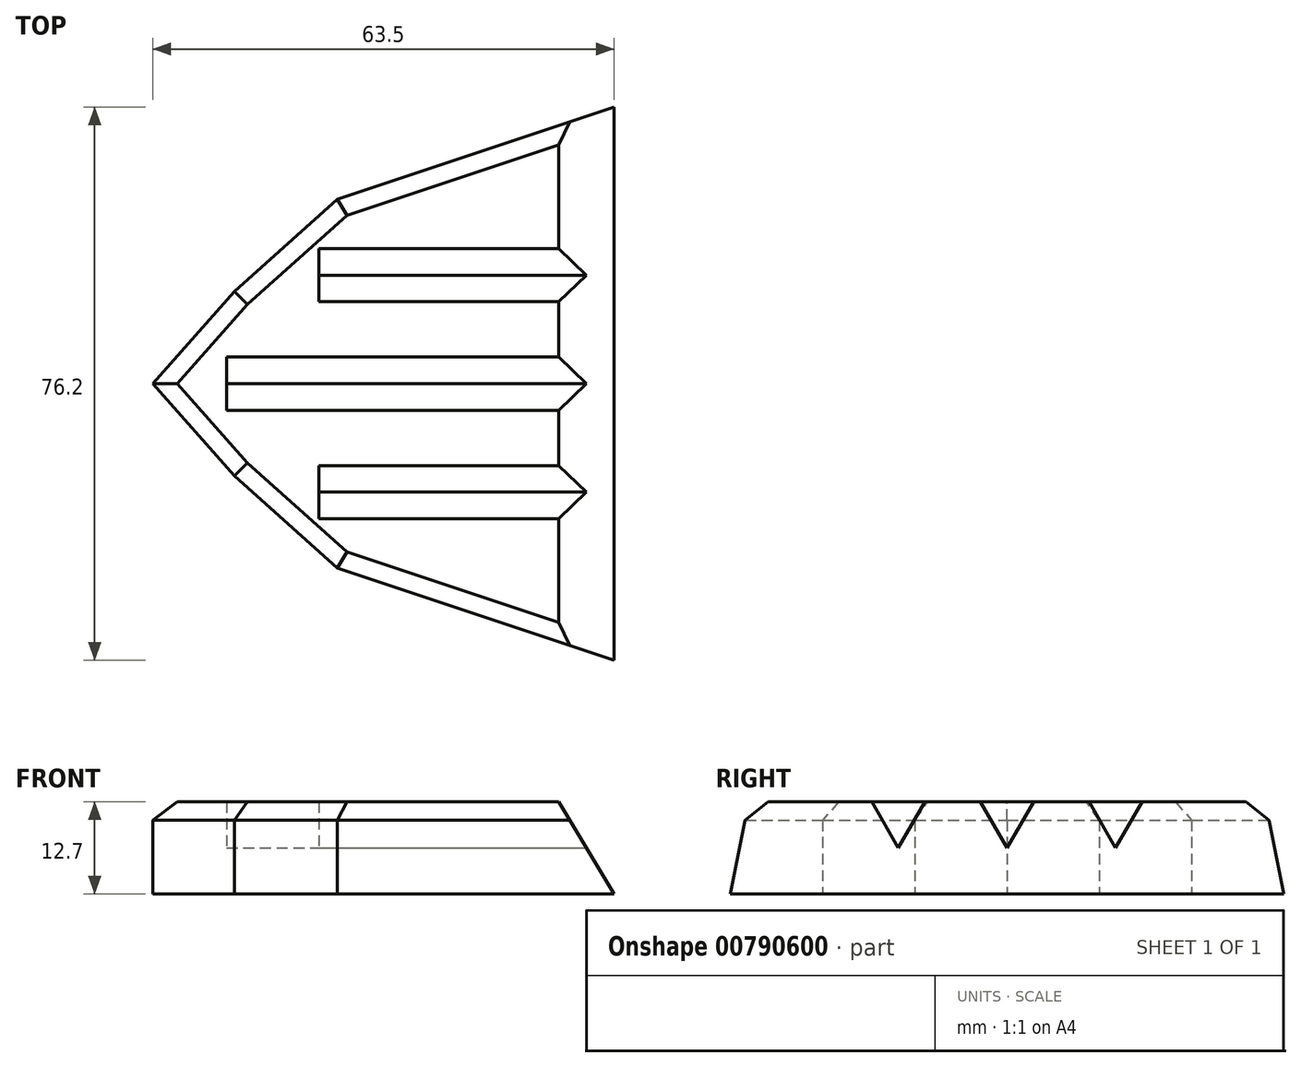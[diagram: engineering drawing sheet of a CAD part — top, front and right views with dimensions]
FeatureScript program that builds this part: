
annotation { "Feature Type Name" : "Feature", "Feature Type Description" : "" }
export const myFeature = defineFeature(function(context is Context, id is Id, definition is map)
    precondition{}
    {
        {
            var Q0;
            Q0=qCreatedBy(makeId("Top.planeOp"),FACE);
            var sketch = newSketch(context, id + "F0", { "sketchPlane" : qUnion([Q0])});
            skLineSegment(sketch, "E0", {"start": v(0, 38.1) * mm, "end": v(-38.1, 25.4) * mm});
            skLineSegment(sketch, "E1", {"start": v(-38.1, 25.4) * mm, "end": v(-52.27, 12.7) * mm});
            skLineSegment(sketch, "E2", {"start": v(-52.27, 12.7) * mm, "end": v(-63.5, 0) * mm});
            skLineSegment(sketch, "E3", {"start": v(-63.5, 0) * mm, "end": v(-52.27, -12.7) * mm});
            skLineSegment(sketch, "E4", {"start": v(-52.27, -12.7) * mm, "end": v(-38.1, -25.4) * mm});
            skLineSegment(sketch, "E5", {"start": v(-38.1, -25.4) * mm, "end": v(0, -38.1) * mm});
            skLineSegment(sketch, "E6", {"start": v(0, -38.1) * mm, "end": v(0, 38.1) * mm});
            skSolve(sketch);
        }
        {
            var Q0;
            Q0=makeQuery(id+"F0.imprint","IMPRINT",FACE,{"disambiguationData":[TD([[makeQuery(id+"F0.imprint","IMPRINT",EDGE,{"derivedFrom":sQuery(id+"F0.wireOp",EDGE,"E0")}),1.0]])]});
            extrude(context, id + "F1", {"entities" : qUnion([Q0]), "depth" : 12.7 * mm, "offsetDistance" : 25.4 * mm});
        }
        {
            var Q0;
            Q0=makeQuery(id+"F1.opExtrude","SWEPT_FACE",FACE,{"disambiguationData":[OSD([sQuery(id+"F0.wireOp",EDGE,"E6")])]});
            var sketch = newSketch(context, id + "F2", { "sketchPlane" : qUnion([Q0])});
            skLineSegment(sketch, "E7", {"start": v(-3.67, 12.7) * mm, "end": v(0, 6.35) * mm});
            skLineSegment(sketch, "E8", {"start": v(0, 6.35) * mm, "end": v(3.67, 12.7) * mm});
            skLineSegment(sketch, "E9", {"start": v(3.67, 12.7) * mm, "end": v(-3.67, 12.7) * mm});
            skLineSegment(sketch, "E10", {"start": v(11.29, 12.7) * mm, "end": v(14.95, 6.35) * mm});
            skLineSegment(sketch, "E11", {"start": v(14.95, 6.35) * mm, "end": v(18.62, 12.7) * mm});
            skLineSegment(sketch, "E12", {"start": v(18.62, 12.7) * mm, "end": v(11.29, 12.7) * mm});
            skLineSegment(sketch, "E13", {"start": v(-11.29, 12.7) * mm, "end": v(-18.62, 12.7) * mm});
            skLineSegment(sketch, "E14", {"start": v(-18.62, 12.7) * mm, "end": v(-14.95, 6.35) * mm});
            skLineSegment(sketch, "E15", {"start": v(-14.95, 6.35) * mm, "end": v(-11.29, 12.7) * mm});
            skSolve(sketch);
        }
        {
            var Q0;
            Q0=makeQuery(id+"F2.imprint","IMPRINT",FACE,{"disambiguationData":[TD([[makeQuery(id+"F2.imprint","IMPRINT",EDGE,{"derivedFrom":sQuery(id+"F2.wireOp",EDGE,"E13")}),-1.0]])]});
            var Q1;
            Q1=makeQuery(id+"F2.imprint","IMPRINT",FACE,{"disambiguationData":[TD([[makeQuery(id+"F2.imprint","IMPRINT",EDGE,{"derivedFrom":sQuery(id+"F2.wireOp",EDGE,"E10")}),1.0]])]});
            extrude(context, id + "F3", {"entities" : qUnion([Q0, Q1]), "operationType" : NewBodyOperationType.REMOVE, "oppositeDirection" : true, "depth" : 40.64 * mm, "offsetDistance" : 25.4 * mm});
        }
        {
            var Q0;
            Q0=makeQuery(id+"F2.imprint","IMPRINT",FACE,{"disambiguationData":[TD([[makeQuery(id+"F2.imprint","IMPRINT",EDGE,{"derivedFrom":sQuery(id+"F2.wireOp",EDGE,"E7")}),1.0]])]});
            extrude(context, id + "F4", {"entities" : qUnion([Q0]), "operationType" : NewBodyOperationType.REMOVE, "oppositeDirection" : true, "depth" : 53.34 * mm, "offsetDistance" : 25.4 * mm});
        }
        {
            var Q0;
            {var subQ0=sQuery(id+"F0.wireOp",EDGE,"E6");var subQ1=sQuery(id+"F0.wireOp",EDGE,"E5");Q0=makeQuery(id+"F3.boolean.opBoolean","SPLIT",EDGE,{"disambiguationData":[TD([makeQuery(id+"F1.opExtrude","SWEPT_FACE",FACE,{"disambiguationData":[OSD([subQ1])]})])],"derivedFrom":makeQuery(id+"F1.opExtrude","CAP_EDGE",EDGE,{"disambiguationData":[OSD([subQ0])],"isStart":false})});}
            var Q1;
            {var subQ0=sQuery(id+"F0.wireOp",EDGE,"E6");var subQ3=makeQuery(id+"F3.opExtrude","SWEPT_FACE",FACE,{"disambiguationData":[OSD([sQuery(id+"F2.wireOp",EDGE,"E15")])]});Q1=makeQuery(id+"F4.boolean.opBoolean","SPLIT",EDGE,{"disambiguationData":[TD([makeQuery(id+"F3.boolean.opBoolean","COPY",FACE,{"derivedFrom":subQ3})])],"derivedFrom":makeQuery(id+"F3.boolean.opBoolean","SPLIT",EDGE,{"disambiguationData":[TD([makeQuery(id+"F3.opExtrude","SWEPT_FACE",FACE,{"disambiguationData":[OSD([sQuery(id+"F2.wireOp",EDGE,"E10")])]})])],"derivedFrom":makeQuery(id+"F1.opExtrude","CAP_EDGE",EDGE,{"disambiguationData":[OSD([subQ0])],"isStart":false})})});}
            var Q2;
            {var subQ0=sQuery(id+"F0.wireOp",EDGE,"E6");var subQ3=makeQuery(id+"F3.opExtrude","SWEPT_FACE",FACE,{"disambiguationData":[OSD([sQuery(id+"F2.wireOp",EDGE,"E10")])]});Q2=makeQuery(id+"F4.boolean.opBoolean","SPLIT",EDGE,{"disambiguationData":[TD([makeQuery(id+"F3.boolean.opBoolean","COPY",FACE,{"derivedFrom":subQ3})])],"derivedFrom":makeQuery(id+"F3.boolean.opBoolean","SPLIT",EDGE,{"disambiguationData":[TD([subQ3])],"derivedFrom":makeQuery(id+"F1.opExtrude","CAP_EDGE",EDGE,{"disambiguationData":[OSD([subQ0])],"isStart":false})})});}
            var Q3;
            {var subQ0=sQuery(id+"F0.wireOp",EDGE,"E0");var subQ1=sQuery(id+"F0.wireOp",EDGE,"E6");Q3=makeQuery(id+"F3.boolean.opBoolean","SPLIT",EDGE,{"disambiguationData":[TD([makeQuery(id+"F1.opExtrude","SWEPT_FACE",FACE,{"disambiguationData":[OSD([subQ0])]})])],"derivedFrom":makeQuery(id+"F1.opExtrude","CAP_EDGE",EDGE,{"disambiguationData":[OSD([subQ1])],"isStart":false})});}
            chamfer(context, id + "F5", {"entities" : qUnion([Q0, Q1, Q2, Q3]), "chamferType" : ChamferType.TWO_OFFSETS, "width1" : 7.62 * mm, "oppositeDirection" : false, "width2" : 12.7 * mm, "tangentPropagation" : true});
        }
        {
            var Q0;
            Q0=makeQuery(id+"F1.opExtrude","CAP_EDGE",EDGE,{"disambiguationData":[OSD([sQuery(id+"F0.wireOp",EDGE,"E5")])],"isStart":false});
            var Q1;
            Q1=makeQuery(id+"F1.opExtrude","CAP_EDGE",EDGE,{"disambiguationData":[OSD([sQuery(id+"F0.wireOp",EDGE,"E4")])],"isStart":false});
            var Q2;
            Q2=makeQuery(id+"F1.opExtrude","CAP_EDGE",EDGE,{"disambiguationData":[OSD([sQuery(id+"F0.wireOp",EDGE,"E3")])],"isStart":false});
            var Q3;
            Q3=makeQuery(id+"F1.opExtrude","CAP_EDGE",EDGE,{"disambiguationData":[OSD([sQuery(id+"F0.wireOp",EDGE,"E2")])],"isStart":false});
            var Q4;
            Q4=makeQuery(id+"F1.opExtrude","CAP_EDGE",EDGE,{"disambiguationData":[OSD([sQuery(id+"F0.wireOp",EDGE,"E1")])],"isStart":false});
            var Q5;
            Q5=makeQuery(id+"F1.opExtrude","CAP_EDGE",EDGE,{"disambiguationData":[OSD([sQuery(id+"F0.wireOp",EDGE,"E0")])],"isStart":false});
            chamfer(context, id + "F6", {"entities" : qUnion([Q0, Q1, Q2, Q3, Q4, Q5]), "width" : 2.54 * mm, "tangentPropagation" : true});
        }
    });
